# Revit family: Tanque compact
name_source: partatom
category: Modelos genéricos
units: mm (PartAtom-declared; Revit-internal decimal feet)

## family parameters
Com base no plano de trabalho = Não
Compartilhado = Não
Corte com vazios quando carregada = Não
Cota do conector redondo = Utilizar diâmetro
Pode hospedar o vergalhão = Não
Ponto de cálculo do ambiente = Não
Sempre na vertical = Sim
Tipo de parte = Normal

## types (1)
- Tanque compact
    Acabamento = Acetinado
    Acessórios inclusos = 1 Válvula Inox 3 1/2'', 1 Tábua 316 x 435 x 18 mm
    Capacidade = 20,5 L
    Descrição = Tanque para Lavar Roupas
    Dimensões = 400 x 340 x 170 mm (Profundidade)
    Elevação padrão = 0 mm  [stored 0 ft]
    Espessura = 0,6 mm
    Fabricante = Tramontina
    Material predominante = Aço Inox
    Modelo = Tanque para Lavar Roupas Compact 20 L
    Modo de instalação = Por baixo
    Referência do produto = 94020/147
    Tipo de material = AISI 304
    URL da ficha técnica = https://assets.tramontina.com.br
    URL do fabricante = tramontina.com.br
    URL do produto = https://www.tramontina.com.br
    URL dos arquivos BIM = tramontina.com.br/biblioteca

note: [stored X ft] marks values corroborated as IEEE doubles in the binary element streams (Revit-internal decimal feet)
